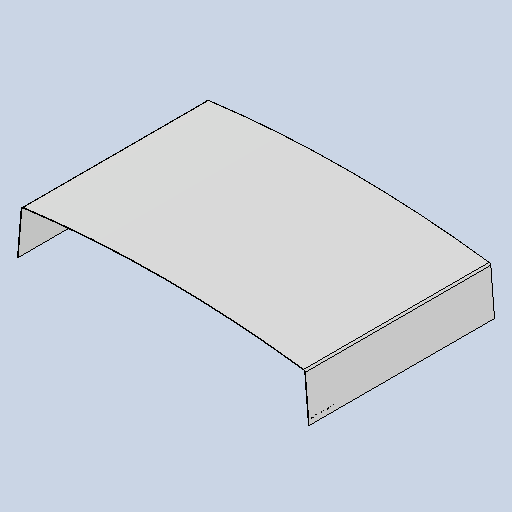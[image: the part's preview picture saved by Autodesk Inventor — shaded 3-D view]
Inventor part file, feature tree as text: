
AUTODESK INVENTOR PART (.ipt)
format: ipt  version: 2025 (Build 290162010, 162A)  size: 335,872 bytes
history: native  units: mm
features: other x7, sheet_metal_op x3, sketch x2, mirror x1
ambient origin geometry x8: Origin, YZ Plane, XZ Plane, XY Plane, X Axis, Y Axis, Z Axis, Center Point
bodies: Body1 (feature_tree)
feature tree (13):
  sheet_metal_op  "Contour Flange2"
  mirror  "Mirror2"
  other  "Mark1"
  other  "A-Side Definition"
  sketch  "Sketch1"  dims[d36=3.0mm]
  other  "Plate2"
  sheet_metal_op  "Bend2"
  sheet_metal_op  "Corner2"
  sketch  "Sketch2"  dims[d37=3.0mm d38=1.5mm d39=6.0mm d40=5.0mm d41=980.0mm d42=5.0mm d43=3.0mm d44=12.0mm d45=3.0mm d46=5.0mm d54=1500.0mm d55=2700.0mm d58=2100.0mm d65=8.0mm d66=8.0mm d78=3.0mm d80=3.0mm d83=8.0mm d113=50.0mm d114=50.0mm d115=3.0mm d121=10.0mm d122=241.9mm d124=16.546129mm d0=1980.030402mm d1=980.0mm]
  other  "Definition1"
  other  "Annotations"
  other  "Linear Dimension 1"
  other  "Linear Dimension 2"
